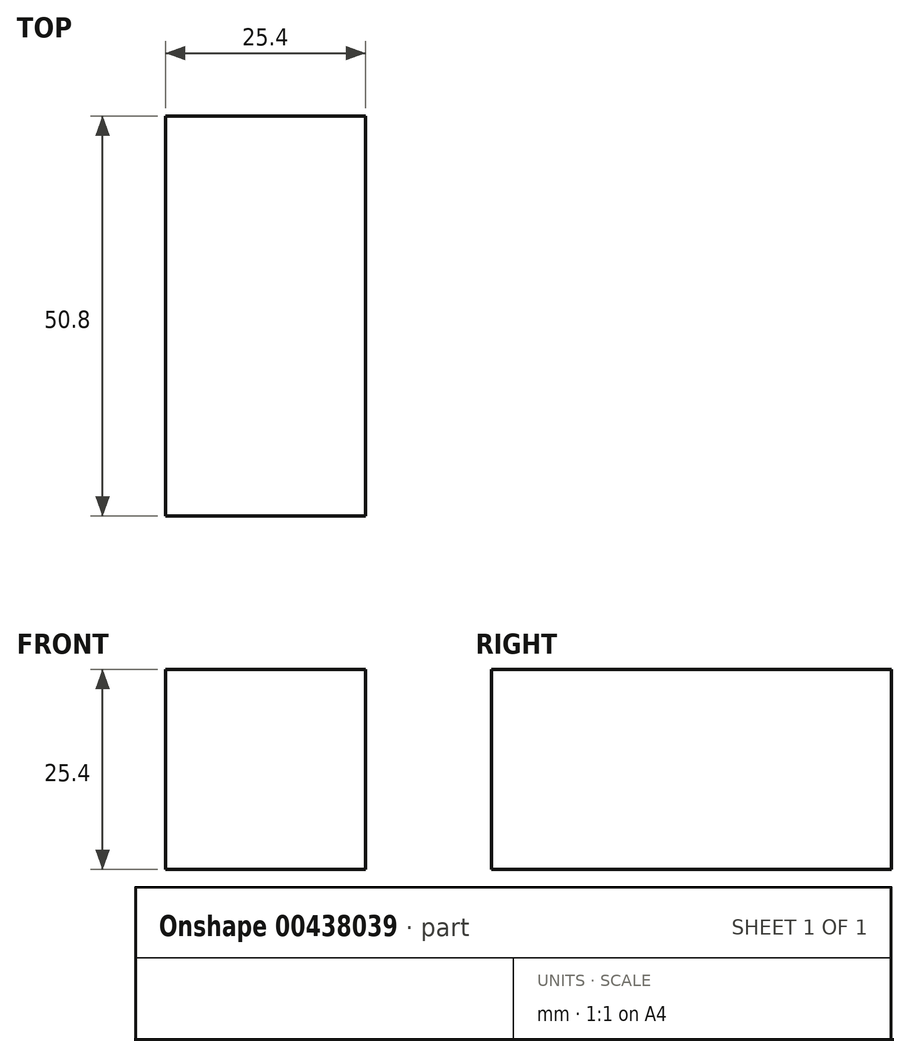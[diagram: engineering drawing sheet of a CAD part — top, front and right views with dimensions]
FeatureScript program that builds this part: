
annotation { "Feature Type Name" : "Feature", "Feature Type Description" : "" }
export const myFeature = defineFeature(function(context is Context, id is Id, definition is map)
    precondition{}
    {
        {
            var Q0;
            Q0=qCreatedBy(makeId("Front.planeOp"),FACE);
            var sketch = newSketch(context, id + "F0", { "sketchPlane" : qUnion([Q0])});
            skLineSegment(sketch, "E0.bottom", {"start": v(0, 0) * mm, "end": v(-25.4, 0) * mm});
            skLineSegment(sketch, "E0.top", {"start": v(0, 25.4) * mm, "end": v(-25.4, 25.4) * mm});
            skLineSegment(sketch, "E0.left", {"start": v(0, 0) * mm, "end": v(0, 25.4) * mm});
            skLineSegment(sketch, "E0.right", {"start": v(-25.4, 0) * mm, "end": v(-25.4, 25.4) * mm});
            skSolve(sketch);
        }
        {
            var Q0;
            Q0 = qSketchRegion(id + "F0", true);
            extrude(context, id + "F1", {"entities" : qUnion([Q0]), "depth" : 50.8 * mm});
        }
    });
